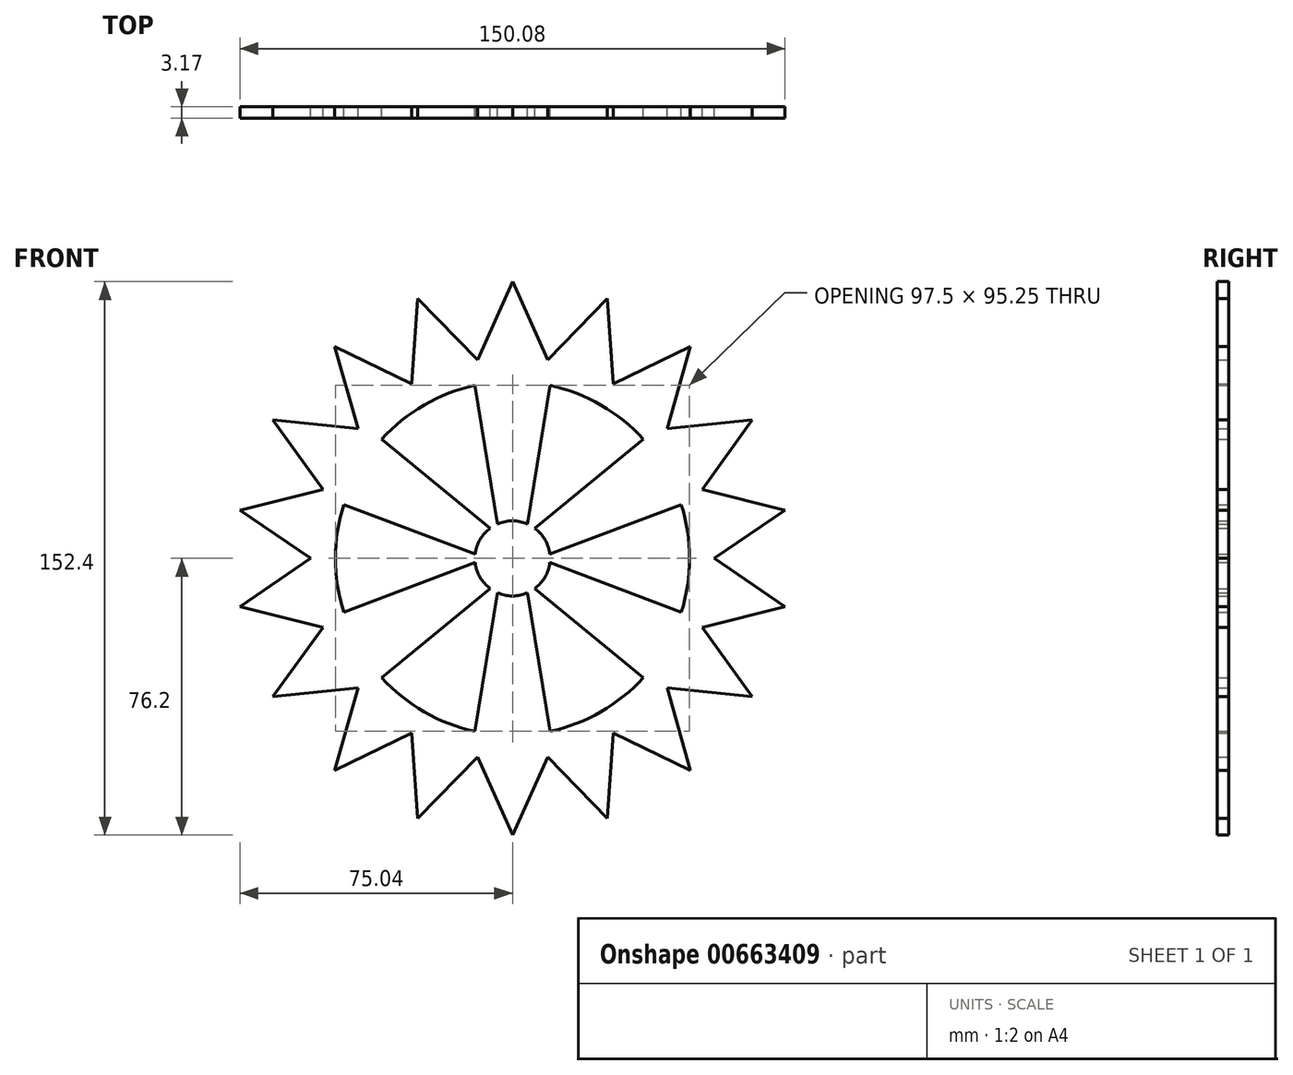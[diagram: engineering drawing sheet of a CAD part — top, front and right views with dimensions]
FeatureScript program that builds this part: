
annotation { "Feature Type Name" : "Feature", "Feature Type Description" : "" }
export const myFeature = defineFeature(function(context is Context, id is Id, definition is map)
    precondition{}
    {
        {
            var Q0;
            Q0=qCreatedBy(makeId("Front.planeOp"),FACE);
            var sketch = newSketch(context, id + "F0", { "sketchPlane" : qUnion([Q0])});
            skCircle(sketch, "E0", {"center": v(0, 0) * mm, "radius": 54.02 * mm});
            skCircle(sketch, "E1", {"center": v(0, 0) * mm, "radius": 76.2 * mm, "construction": true});
            skLineSegment(sketch, "E2", {"start": v(0, 76.2) * mm, "end": v(0, -76.2) * mm, "construction": true});
            skLineSegment(sketch, "E3", {"start": v(0, 76.2) * mm, "end": v(10.4, 53.01) * mm});
            skLineSegment(sketch, "E4.MirrorCS", {"start": v(0, 76.2) * mm, "end": v(-10.4, 53.01) * mm});
            skLineSegment(sketch, "E5.1.0", {"start": v(26.06, 71.6) * mm, "end": v(8.36, 53.37) * mm});
            skLineSegment(sketch, "E5.1.1", {"start": v(26.06, 71.6) * mm, "end": v(27.9, 46.26) * mm});
            skLineSegment(sketch, "E5.2.0", {"start": v(48.98, 58.37) * mm, "end": v(26.11, 47.3) * mm});
            skLineSegment(sketch, "E5.2.1", {"start": v(48.98, 58.37) * mm, "end": v(42.04, 33.93) * mm});
            skLineSegment(sketch, "E5.3.0", {"start": v(66, 38.1) * mm, "end": v(40.71, 35.51) * mm});
            skLineSegment(sketch, "E5.3.1", {"start": v(66, 38.1) * mm, "end": v(51.11, 17.5) * mm});
            skLineSegment(sketch, "E5.4.0", {"start": v(75.04, 13.23) * mm, "end": v(50.4, 19.45) * mm});
            skLineSegment(sketch, "E5.4.1", {"start": v(75.04, 13.23) * mm, "end": v(54.01, -1.04) * mm});
            skLineSegment(sketch, "E5.5.0", {"start": v(75.04, -13.23) * mm, "end": v(54.01, 1.04) * mm});
            skLineSegment(sketch, "E5.5.1", {"start": v(75.04, -13.23) * mm, "end": v(50.4, -19.45) * mm});
            skLineSegment(sketch, "E5.6.0", {"start": v(66, -38.1) * mm, "end": v(51.11, -17.5) * mm});
            skLineSegment(sketch, "E5.6.1", {"start": v(66, -38.1) * mm, "end": v(40.71, -35.51) * mm});
            skLineSegment(sketch, "E5.7.0", {"start": v(48.98, -58.37) * mm, "end": v(42.04, -33.93) * mm});
            skLineSegment(sketch, "E5.7.1", {"start": v(48.98, -58.37) * mm, "end": v(26.11, -47.3) * mm});
            skLineSegment(sketch, "E5.8.0", {"start": v(26.06, -71.6) * mm, "end": v(27.9, -46.26) * mm});
            skLineSegment(sketch, "E5.8.1", {"start": v(26.06, -71.6) * mm, "end": v(8.36, -53.37) * mm});
            skLineSegment(sketch, "E5.9.0", {"start": v(0, -76.2) * mm, "end": v(10.4, -53.01) * mm});
            skLineSegment(sketch, "E5.9.1", {"start": v(0, -76.2) * mm, "end": v(-10.4, -53.01) * mm});
            skLineSegment(sketch, "E5.10.0", {"start": v(-26.06, -71.6) * mm, "end": v(-8.36, -53.37) * mm});
            skLineSegment(sketch, "E5.10.1", {"start": v(-26.06, -71.6) * mm, "end": v(-27.9, -46.26) * mm});
            skLineSegment(sketch, "E5.11.0", {"start": v(-48.98, -58.37) * mm, "end": v(-26.11, -47.3) * mm});
            skLineSegment(sketch, "E5.11.1", {"start": v(-48.98, -58.37) * mm, "end": v(-42.04, -33.93) * mm});
            skLineSegment(sketch, "E5.12.0", {"start": v(-66, -38.1) * mm, "end": v(-40.71, -35.51) * mm});
            skLineSegment(sketch, "E5.12.1", {"start": v(-66, -38.1) * mm, "end": v(-51.11, -17.5) * mm});
            skLineSegment(sketch, "E5.13.0", {"start": v(-75.04, -13.23) * mm, "end": v(-50.4, -19.45) * mm});
            skLineSegment(sketch, "E5.13.1", {"start": v(-75.04, -13.23) * mm, "end": v(-54.01, 1.04) * mm});
            skLineSegment(sketch, "E5.14.0", {"start": v(-75.04, 13.23) * mm, "end": v(-54.01, -1.04) * mm});
            skLineSegment(sketch, "E5.14.1", {"start": v(-75.04, 13.23) * mm, "end": v(-50.4, 19.45) * mm});
            skLineSegment(sketch, "E5.15.0", {"start": v(-66, 38.1) * mm, "end": v(-51.11, 17.5) * mm});
            skLineSegment(sketch, "E5.15.1", {"start": v(-66, 38.1) * mm, "end": v(-40.71, 35.51) * mm});
            skLineSegment(sketch, "E5.16.0", {"start": v(-48.98, 58.37) * mm, "end": v(-42.04, 33.93) * mm});
            skLineSegment(sketch, "E5.16.1", {"start": v(-48.98, 58.37) * mm, "end": v(-26.11, 47.3) * mm});
            skLineSegment(sketch, "E5.17.0", {"start": v(-26.06, 71.6) * mm, "end": v(-27.9, 46.26) * mm});
            skLineSegment(sketch, "E5.17.1", {"start": v(-26.06, 71.6) * mm, "end": v(-8.36, 53.37) * mm});
            skLineSegment(sketch, "E6", {"start": v(0, 54.02) * mm, "end": v(0, -54.02) * mm});
            skCircle(sketch, "E7", {"center": v(0, 0) * mm, "radius": 48.75 * mm});
            skCircle(sketch, "E8", {"center": v(0, 0) * mm, "radius": 10.33 * mm});
            skLineSegment(sketch, "E9", {"start": v(10.4, 47.63) * mm, "end": v(4.13, 9.46) * mm});
            skLineSegment(sketch, "E10.MirrorCS", {"start": v(-10.4, 47.63) * mm, "end": v(-4.13, 9.46) * mm});
            skLineSegment(sketch, "E11.1.0", {"start": v(46.45, 14.8) * mm, "end": v(10.26, 1.15) * mm});
            skLineSegment(sketch, "E11.1.1", {"start": v(36.05, 32.82) * mm, "end": v(6.13, 8.31) * mm});
            skLineSegment(sketch, "E11.2.0", {"start": v(36.05, -32.82) * mm, "end": v(6.13, -8.31) * mm});
            skLineSegment(sketch, "E11.2.1", {"start": v(46.45, -14.8) * mm, "end": v(10.26, -1.15) * mm});
            skLineSegment(sketch, "E11.3.0", {"start": v(-10.4, -47.63) * mm, "end": v(-4.13, -9.46) * mm});
            skLineSegment(sketch, "E11.3.1", {"start": v(10.4, -47.63) * mm, "end": v(4.13, -9.46) * mm});
            skLineSegment(sketch, "E11.4.0", {"start": v(-46.45, -14.8) * mm, "end": v(-10.26, -1.15) * mm});
            skLineSegment(sketch, "E11.4.1", {"start": v(-36.05, -32.82) * mm, "end": v(-6.13, -8.31) * mm});
            skLineSegment(sketch, "E11.5.0", {"start": v(-36.05, 32.82) * mm, "end": v(-6.13, 8.31) * mm});
            skLineSegment(sketch, "E11.5.1", {"start": v(-46.45, 14.8) * mm, "end": v(-10.26, 1.15) * mm});
            skLineSegment(sketch, "E11.anchor1", {"start": v(0, 0) * mm, "end": v(4.13, 9.46) * mm, "construction": true});
            skLineSegment(sketch, "E11.anchor2", {"start": v(0, 0) * mm, "end": v(-6.13, 8.31) * mm, "construction": true});
            skCircle(sketch, "E12", {"center": v(0, 0) * mm, "radius": 7.02 * mm});
            skSolve(sketch);
        }
        {
            var Q0;
            Q0 = qSketchRegion(id + "F0", true);
            var Q1;
            {var subQ0=sQuery(id+"F0.wireOp",EDGE,"E11.5.0");Q1=makeQuery(id+"F0.imprint","IMPRINT",FACE,{"disambiguationData":[TD([[makeQuery(id+"F0.imprint","IMPRINT",EDGE,{"derivedFrom":subQ0}),-1.0]])]});}
            var Q2;
            {var subQ0=sQuery(id+"F0.wireOp",EDGE,"E0");var subQ22=makeQuery(id+"F0.imprint","INTERSECT",VERTEX,{"derivedFrom":[subQ0,sQuery(id+"F0.wireOp",EDGE,"E5.17.1")]});Q2=makeQuery(id+"F0.imprint","IMPRINT",FACE,{"disambiguationData":[TD([[makeQuery(id+"F0.imprint","IMPRINT",EDGE,{"disambiguationData":[TD([[subQ22,1.0]])],"derivedFrom":subQ0}),1.0]])]});}
            var Q3;
            {var subQ1=sQuery(id+"F0.wireOp",EDGE,"E0");var subQ21=makeQuery(id+"F0.imprint","INTERSECT",VERTEX,{"derivedFrom":[subQ1,sQuery(id+"F0.wireOp",EDGE,"E5.3.1")]});Q3=makeQuery(id+"F0.imprint","IMPRINT",FACE,{"disambiguationData":[TD([[makeQuery(id+"F0.imprint","IMPRINT",EDGE,{"disambiguationData":[TD([[subQ21,1.0]])],"derivedFrom":subQ1}),1.0]])]});}
            var Q4;
            {var subQ5=sQuery(id+"F0.wireOp",EDGE,"E9");Q4=makeQuery(id+"F0.imprint","IMPRINT",FACE,{"disambiguationData":[TD([[makeQuery(id+"F0.imprint","IMPRINT",EDGE,{"derivedFrom":subQ5}),-1.0]])]});}
            var Q5;
            {var subQ5=sQuery(id+"F0.wireOp",EDGE,"E10.MirrorCS");Q5=makeQuery(id+"F0.imprint","IMPRINT",FACE,{"disambiguationData":[TD([[makeQuery(id+"F0.imprint","IMPRINT",EDGE,{"derivedFrom":subQ5}),1.0]])]});}
            var Q6;
            {var subQ0=sQuery(id+"F0.wireOp",EDGE,"E11.1.0");Q6=makeQuery(id+"F0.imprint","IMPRINT",FACE,{"disambiguationData":[TD([[makeQuery(id+"F0.imprint","IMPRINT",EDGE,{"derivedFrom":subQ0}),-1.0]])]});}
            var Q7;
            {var subQ0=sQuery(id+"F0.wireOp",EDGE,"E11.2.0");Q7=makeQuery(id+"F0.imprint","IMPRINT",FACE,{"disambiguationData":[TD([[makeQuery(id+"F0.imprint","IMPRINT",EDGE,{"derivedFrom":subQ0}),-1.0]])]});}
            var Q8;
            {var subQ5=sQuery(id+"F0.wireOp",EDGE,"E11.3.1");Q8=makeQuery(id+"F0.imprint","IMPRINT",FACE,{"disambiguationData":[TD([[makeQuery(id+"F0.imprint","IMPRINT",EDGE,{"derivedFrom":subQ5}),1.0]])]});}
            var Q9;
            {var subQ0=sQuery(id+"F0.wireOp",EDGE,"E11.4.0");Q9=makeQuery(id+"F0.imprint","IMPRINT",FACE,{"disambiguationData":[TD([[makeQuery(id+"F0.imprint","IMPRINT",EDGE,{"derivedFrom":subQ0}),-1.0]])]});}
            var Q10;
            {var subQ5=sQuery(id+"F0.wireOp",EDGE,"E11.3.0");Q10=makeQuery(id+"F0.imprint","IMPRINT",FACE,{"disambiguationData":[TD([[makeQuery(id+"F0.imprint","IMPRINT",EDGE,{"derivedFrom":subQ5}),-1.0]])]});}
            var Q11;
            {var subQ0=sQuery(id+"F0.wireOp",EDGE,"E8");var subQ4=sQuery(id+"F0.wireOp",EDGE,"E6");var subQ7=makeQuery(id+"F0.imprint","INTERSECT",VERTEX,{"disambiguationData":[OD(0.0)],"derivedFrom":[subQ4,subQ0]});Q11=makeQuery(id+"F0.imprint","IMPRINT",FACE,{"disambiguationData":[TD([[makeQuery(id+"F0.imprint","IMPRINT",EDGE,{"disambiguationData":[TD([[subQ7,-1.0]])],"derivedFrom":subQ4}),-1.0]])]});}
            var Q12;
            {var subQ0=sQuery(id+"F0.wireOp",EDGE,"E8");var subQ6=sQuery(id+"F0.wireOp",EDGE,"E6");var subQ12=makeQuery(id+"F0.imprint","INTERSECT",VERTEX,{"disambiguationData":[OD(0.0)],"derivedFrom":[subQ6,subQ0]});Q12=makeQuery(id+"F0.imprint","IMPRINT",FACE,{"disambiguationData":[TD([[makeQuery(id+"F0.imprint","IMPRINT",EDGE,{"disambiguationData":[TD([[subQ12,-1.0]])],"derivedFrom":subQ6}),1.0]])]});}
            extrude(context, id + "F1", {"entities" : qUnion([Q0, Q1, Q2, Q3, Q4, Q5, Q6, Q7, Q8, Q9, Q10, Q11, Q12]), "depth" : 3.17 * mm, "offsetDistance" : 25.4 * mm});
        }
    });
